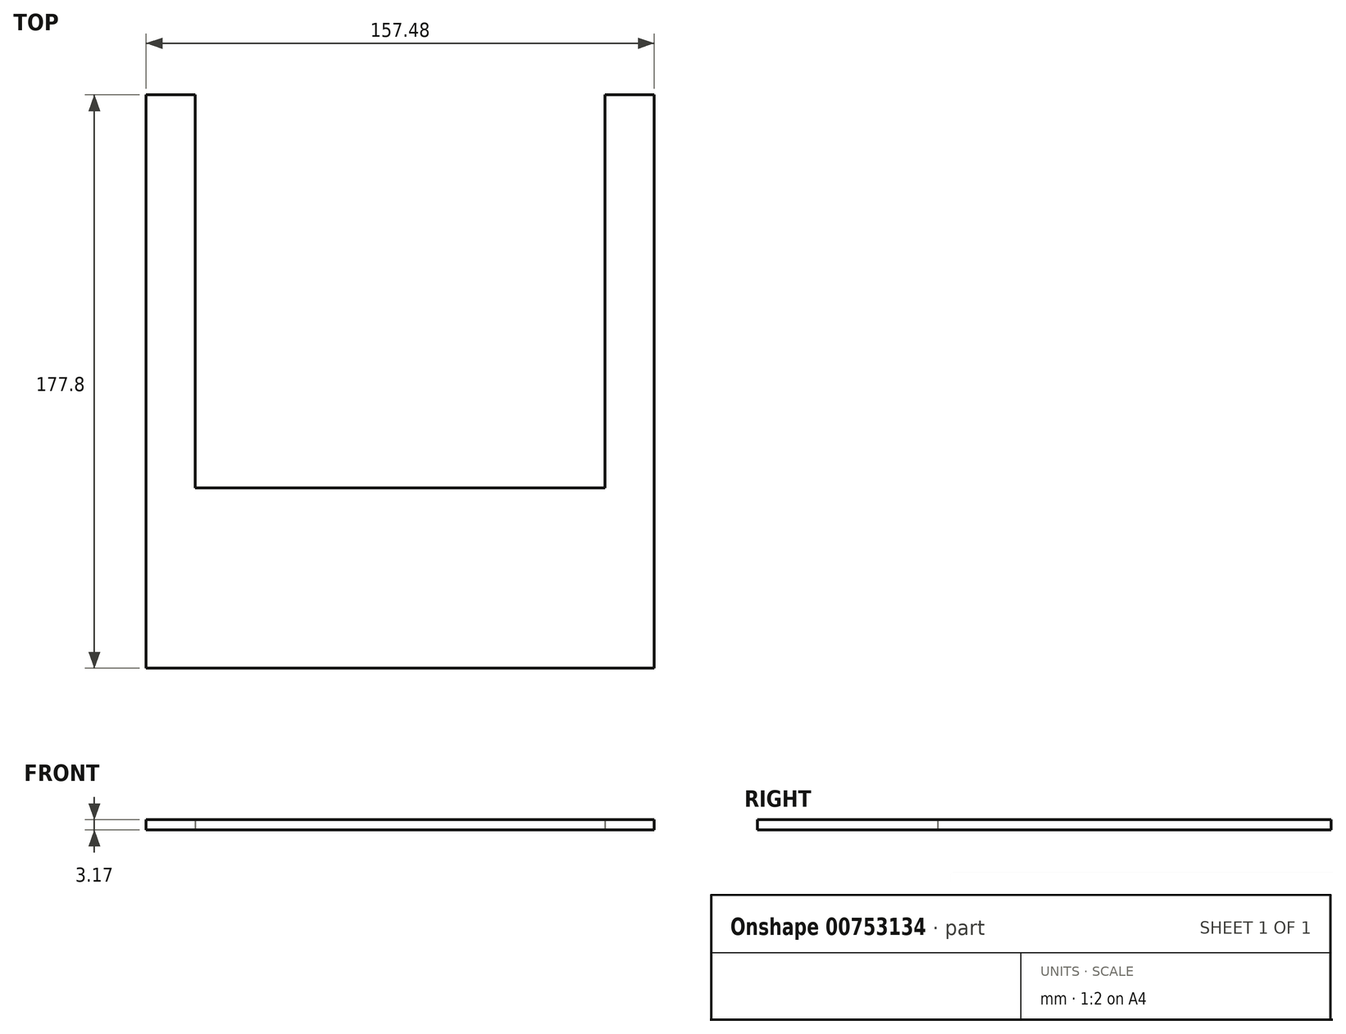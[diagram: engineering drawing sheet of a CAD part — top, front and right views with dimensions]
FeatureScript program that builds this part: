
annotation { "Feature Type Name" : "Feature", "Feature Type Description" : "" }
export const myFeature = defineFeature(function(context is Context, id is Id, definition is map)
    precondition{}
    {
        {
            var Q0;
            Q0=qCreatedBy(makeId("Top.planeOp"),FACE);
            var sketch = newSketch(context, id + "F0", { "sketchPlane" : qUnion([Q0])});
            skLineSegment(sketch, "E0.bottom", {"start": v(-87.12, 101.04) * mm, "end": v(-71.88, 101.04) * mm});
            skLineSegment(sketch, "E0.top", {"start": v(-87.12, -76.76) * mm, "end": v(70.36, -76.76) * mm});
            skLineSegment(sketch, "E0.left", {"start": v(-87.12, 101.04) * mm, "end": v(-87.12, -76.76) * mm});
            skLineSegment(sketch, "E0.right", {"start": v(70.36, 101.04) * mm, "end": v(70.36, -76.76) * mm});
            skLineSegment(sketch, "E1.top", {"start": v(-71.88, -20.88) * mm, "end": v(55.12, -20.88) * mm});
            skLineSegment(sketch, "E1.left", {"start": v(-71.88, 101.04) * mm, "end": v(-71.88, -20.88) * mm});
            skLineSegment(sketch, "E1.right", {"start": v(55.12, 101.04) * mm, "end": v(55.12, -20.88) * mm});
            skLineSegment(sketch, "E2.trimOffspring", {"start": v(55.12, 101.04) * mm, "end": v(70.36, 101.04) * mm});
            skSolve(sketch);
        }
        {
            var Q0;
            Q0=makeQuery(id+"F0.imprint","IMPRINT",FACE,{"disambiguationData":[TD([[makeQuery(id+"F0.imprint","IMPRINT",EDGE,{"derivedFrom":sQuery(id+"F0.wireOp",EDGE,"E0.bottom")}),-1.0]])]});
            extrude(context, id + "F1", {"entities" : qUnion([Q0]), "depth" : 3.17 * mm, "offsetDistance" : 25.4 * mm});
        }
    });
